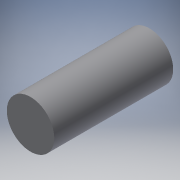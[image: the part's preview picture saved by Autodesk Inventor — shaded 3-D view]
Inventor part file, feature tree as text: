
AUTODESK INVENTOR PART (.ipt)
format: ipt  version: 2018.1 (Build 221171000, 171)  size: 92,160 bytes
history: native  units: mm
features: extrude x1, sketch x1
ambient origin geometry x8: Origin, YZ Plane, XZ Plane, XY Plane, X Axis, Y Axis, Z Axis, Center Point
bodies: Solid1 (feature_tree)
feature tree (2):
  extrude  "Extrusion1"  Depth=50.0mm TaperAngle=0.0deg
  sketch  "Sketch1"  dims[d0=19.94mm d1=50.0mm d2=0.0mm]
